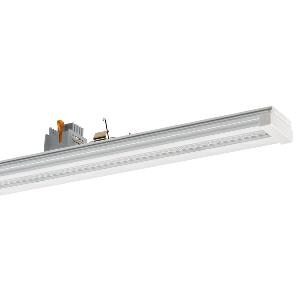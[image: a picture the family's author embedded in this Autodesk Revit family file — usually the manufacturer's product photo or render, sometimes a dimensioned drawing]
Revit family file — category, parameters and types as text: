
# Revit family: conveo_-_cvg_4500_850_xn-l_da_7_226848389-00804977_8dca
name_source: partatom
category: Lighting Fixtures
units: mm (PartAtom-declared; Revit-internal decimal feet)

## family parameters
Cut with Voids When Loaded = No
Host = Face
Light Source = No
Part Type = Normal
Room Calculation Point = No
Round Connector Dimension = Use Diameter
Shared = No

## types (1)
- CONVEO - CVG 4500/850/xN-L/DA/7 (1 x LED, 4650 lm, 5000K)
    Apparent Load = 27 VA
    Approval mark = CE
    CIE Flux Codes = 84 95 99 100 100
    Color Rendering = 80-89
    Color Temperature = 5000K
    Control Gear = Electronic ballast
    Default Elevation = 1800 mm
    Description = CVG 4500/850/xN-L/DA/7|Continuous-row system|light source: LED|work equipment: Adjustable electronic ballast, digital DALI|connected load: 220-240 V, 50-60 Hz|Power consumption: approx. 27 W|luminous flux: 4650 lm|luminous efficacy: 172 lm/W|colour temperature: Cold white, ca. 5000 K|color rendering index (CRI): >= 80|chromaticity tolerance:  3 SDCM|System of protection: IP 54|class of protection: I|technology: Continuously dimmable|luminaire body|material: Aluminium|surface: Powder coatet|colour: White|lamp cover: Acrylic (PMMA), Satine|weight (net): approx. 1.9 kg|Fastening: Available separately|maximum ambient temperature: 50 ░C|glare control: Lens optics|Approval mark: VDE - ENEC|
    Frequency = 50 Hz
    Height = 70 mm
    Lamp = 1 x LED
    Lamp Light Flux = 4650 lm
    Lamp count = 1
    Length = 1500 mm
    Luminous efficacy = 172 lm/W
    Manufacturer = Waldmann
    ModVariant = No
    Model = 226848389-00804977
    Mounting Place = Ceiling
    Mounting Type = Pendant
    Number of Poles = 1
    OnlyDefault = Yes
    Power Factor = 1
    Product Name = CONVEO - CVG 4500/850/xN-L/DA/7
    Product group = Continuous-row system (industry)
    ProductGroupID = 301
    Protection Class = Protection class I
    Protection Degree = IP 54
    RLX_Detail_Level = 1
    RlxData = <blob elided: 100977 chars, md5=45138523>
    Socket = socket
    Standby Power = 0 W
    System Light Flux = 4650 lm
    System Power = 27 W
    Type Comments = Product without accessories
    Type Image = 226848259-00804964_1l7.jpg
    URL = http://relux.com
    VarID = ---
    Voltage = 230 V
    Voltage Range = 220-240 V
    Weight = 0.00 kg
    Width = 64 mm

## geometry (parser evidence)
native form markers: Blend x4, Sweep x11
no freeform markers — native parametric forms only
